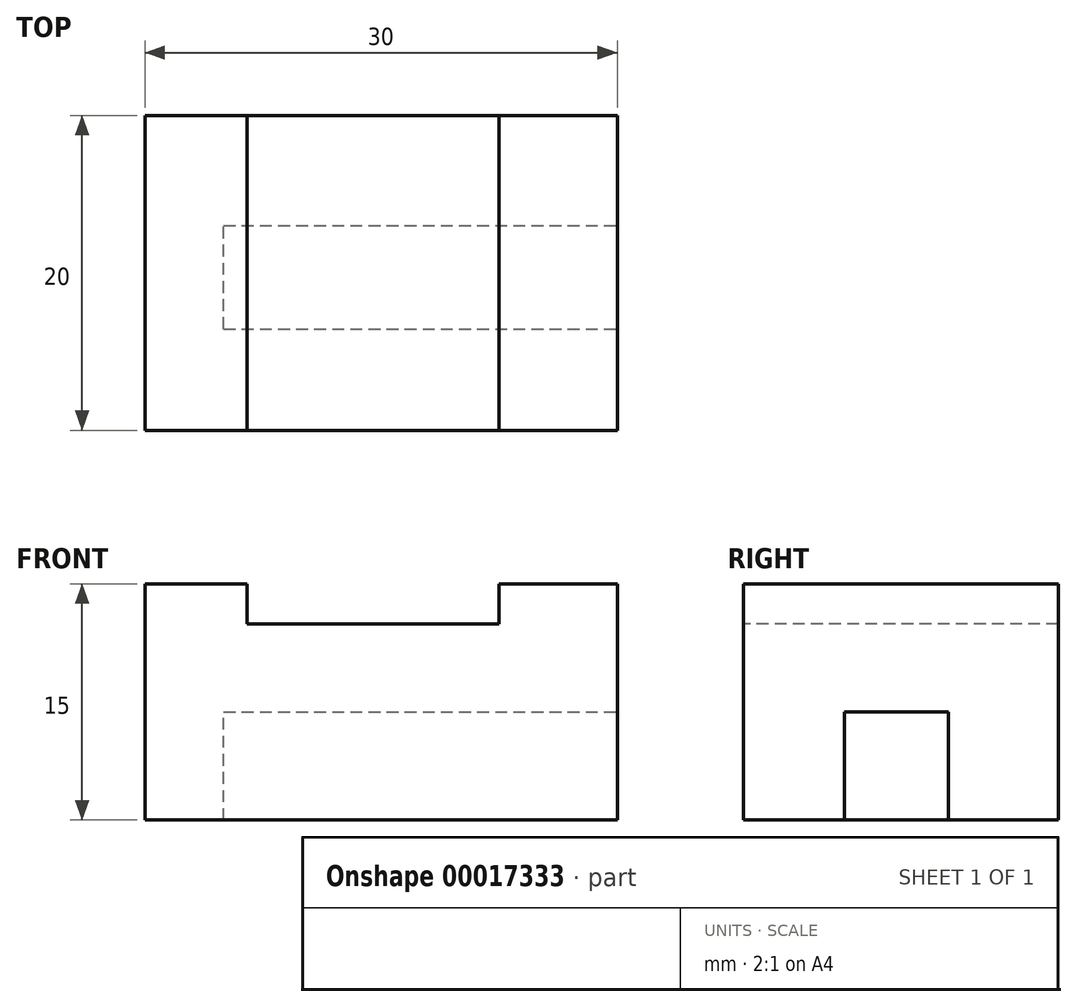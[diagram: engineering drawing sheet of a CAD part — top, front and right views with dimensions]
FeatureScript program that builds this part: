
annotation { "Feature Type Name" : "Feature", "Feature Type Description" : "" }
export const myFeature = defineFeature(function(context is Context, id is Id, definition is map)
    precondition{}
    {
        {
            var Q0;
            Q0=qCreatedBy(makeId("Front.planeOp"),FACE);
            var sketch = newSketch(context, id + "F0", { "sketchPlane" : qUnion([Q0])});
            skLineSegment(sketch, "E0.bottom", {"start": v(-8.93, 29.72) * mm, "end": v(21.07, 29.72) * mm});
            skLineSegment(sketch, "E0.top", {"start": v(-8.93, 14.72) * mm, "end": v(21.07, 14.72) * mm});
            skLineSegment(sketch, "E0.left", {"start": v(-8.93, 29.72) * mm, "end": v(-8.93, 14.72) * mm});
            skLineSegment(sketch, "E0.right", {"start": v(21.07, 29.72) * mm, "end": v(21.07, 14.72) * mm});
            skSolve(sketch);
        }
        {
            var Q0;
            Q0=makeQuery(id+"F0.imprint","IMPRINT",FACE,{"disambiguationData":[TD([[makeQuery(id+"F0.imprint","IMPRINT",EDGE,{"derivedFrom":sQuery(id+"F0.wireOp",EDGE,"E0.bottom")}),-1.0]])]});
            extrude(context, id + "F1", {"entities" : qUnion([Q0]), "depth" : 20 * mm});
        }
        {
            var Q0;
            Q0=makeQuery(id+"F1.opExtrude","CAP_FACE",FACE,{"disambiguationData":[OSD([sQuery(id+"F0.wireOp",EDGE,"E0.bottom"),sQuery(id+"F0.wireOp",EDGE,"E0.top"),sQuery(id+"F0.wireOp",EDGE,"E0.left"),sQuery(id+"F0.wireOp",EDGE,"E0.right")])],"isStart":false});
            var sketch = newSketch(context, id + "F2", { "sketchPlane" : qUnion([Q0])});
            skLineSegment(sketch, "E1.bottom", {"start": v(-2.45, 29.72) * mm, "end": v(13.57, 29.72) * mm});
            skLineSegment(sketch, "E1.top", {"start": v(-2.45, 27.18) * mm, "end": v(13.57, 27.18) * mm});
            skLineSegment(sketch, "E1.left", {"start": v(-2.45, 29.72) * mm, "end": v(-2.45, 27.18) * mm});
            skLineSegment(sketch, "E1.right", {"start": v(13.57, 29.72) * mm, "end": v(13.57, 27.18) * mm});
            skSolve(sketch);
        }
        {
            var Q0;
            Q0=makeQuery(id+"F2.imprint","IMPRINT",FACE,{"disambiguationData":[TD([[makeQuery(id+"F2.imprint","IMPRINT",EDGE,{"derivedFrom":sQuery(id+"F2.wireOp",EDGE,"E1.bottom")}),-1.0]])]});
            extrude(context, id + "F3", {"entities" : qUnion([Q0]), "operationType" : NewBodyOperationType.REMOVE, "oppositeDirection" : true, "depth" : 25 * mm});
        }
        {
            var Q0;
            Q0=makeQuery(id+"F1.opExtrude","SWEPT_FACE",FACE,{"disambiguationData":[OSD([sQuery(id+"F0.wireOp",EDGE,"E0.right")])]});
            var sketch = newSketch(context, id + "F4", { "sketchPlane" : qUnion([Q0])});
            skLineSegment(sketch, "E2.bottom", {"start": v(-13.56, 14.72) * mm, "end": v(-6.98, 14.72) * mm});
            skLineSegment(sketch, "E2.top", {"start": v(-13.56, 21.59) * mm, "end": v(-6.98, 21.59) * mm});
            skLineSegment(sketch, "E2.left", {"start": v(-13.56, 14.72) * mm, "end": v(-13.56, 21.59) * mm});
            skLineSegment(sketch, "E2.right", {"start": v(-6.98, 14.72) * mm, "end": v(-6.98, 21.59) * mm});
            skSolve(sketch);
        }
        {
            var Q0;
            Q0=makeQuery(id+"F4.imprint","IMPRINT",FACE,{"disambiguationData":[TD([[makeQuery(id+"F4.imprint","IMPRINT",EDGE,{"derivedFrom":sQuery(id+"F4.wireOp",EDGE,"E2.bottom")}),1.0]])]});
            extrude(context, id + "F5", {"entities" : qUnion([Q0]), "operationType" : NewBodyOperationType.REMOVE, "oppositeDirection" : true, "depth" : 25 * mm});
        }
    });
